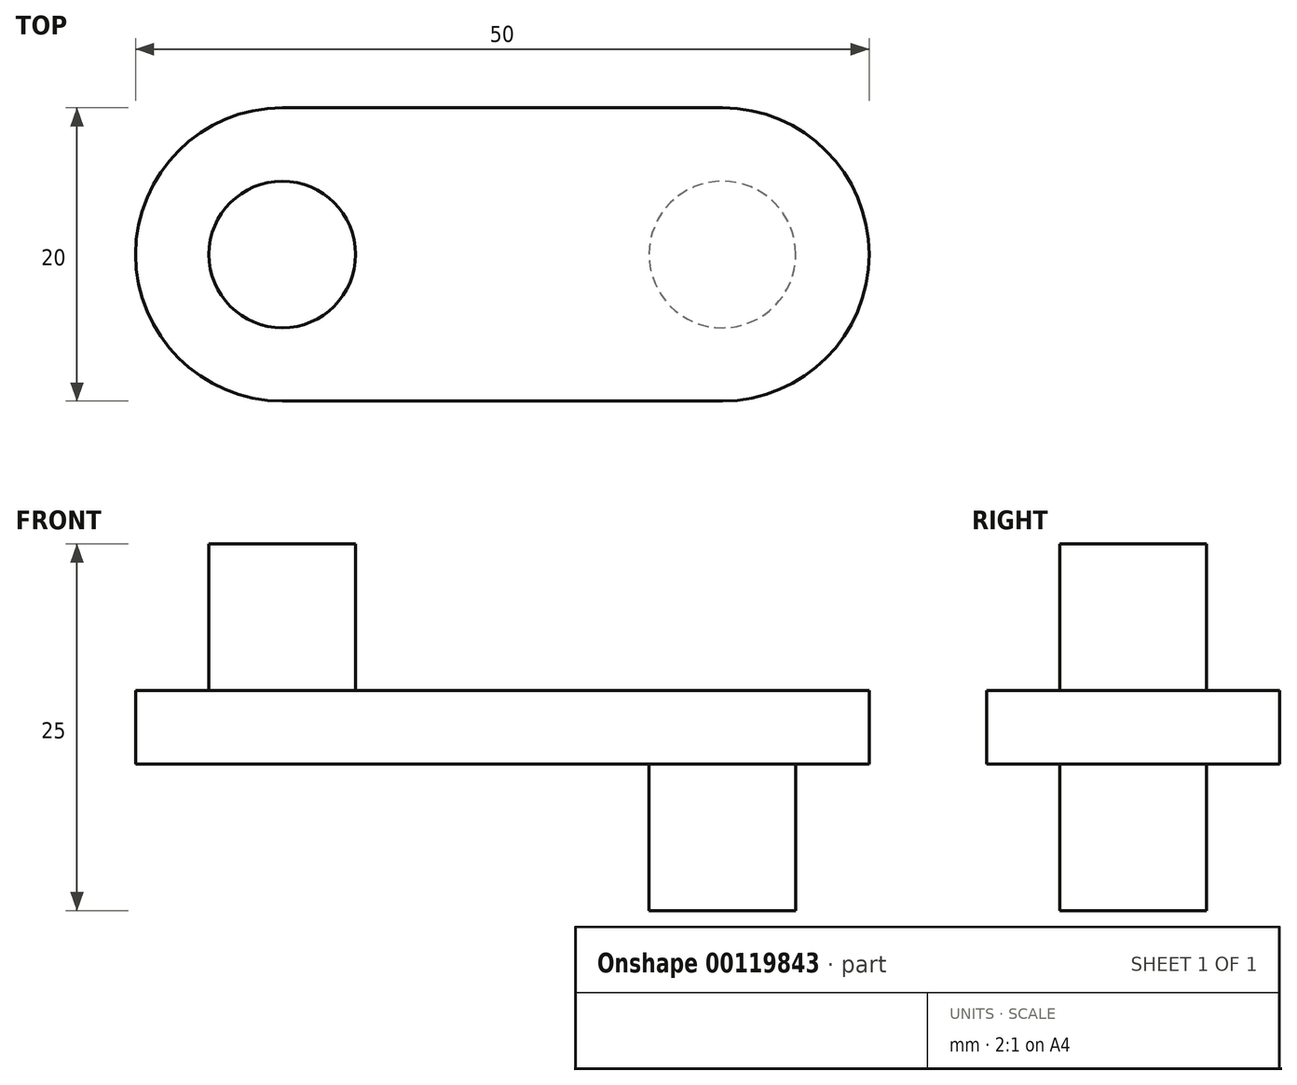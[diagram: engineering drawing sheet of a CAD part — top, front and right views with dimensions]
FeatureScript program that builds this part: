
annotation { "Feature Type Name" : "Feature", "Feature Type Description" : "" }
export const myFeature = defineFeature(function(context is Context, id is Id, definition is map)
    precondition{}
    {
        {
            var Q0;
            Q0=qCreatedBy(makeId("Top.planeOp"),FACE);
            var sketch = newSketch(context, id + "F0", { "sketchPlane" : qUnion([Q0])});
            skLineSegment(sketch, "E0", {"start": v(0, 43) * mm, "end": v(0, -24.5) * mm, "construction": true});
            skLineSegment(sketch, "E1", {"start": v(-26.57, 0) * mm, "end": v(38.25, 0) * mm, "construction": true});
            skLineSegment(sketch, "E2", {"start": v(0, 0) * mm, "end": v(30, 0) * mm});
            skLineSegment(sketch, "E3", {"start": v(0, 20) * mm, "end": v(30, 20) * mm});
            skLineSegment(sketch, "E4", {"start": v(30, 35.47) * mm, "end": v(30, -14.28) * mm, "construction": true});
            skArc(sketch, "E5", {"start": v(0, 20) * mm, "mid": v(-10, 10) * mm, "end": v(0, 0) * mm});
            skArc(sketch, "E6", {"start": v(30, 0) * mm, "mid": v(40, 10) * mm, "end": v(30, 20) * mm});
            skCircle(sketch, "E7", {"center": v(0, 10) * mm, "radius": 5 * mm});
            skCircle(sketch, "E8", {"center": v(30, 10) * mm, "radius": 5 * mm});
            skSolve(sketch);
        }
        {
            var Q0;
            Q0=makeQuery(id+"F0.imprint","IMPRINT",FACE,{"disambiguationData":[TD([[makeQuery(id+"F0.imprint","IMPRINT",EDGE,{"derivedFrom":sQuery(id+"F0.wireOp",EDGE,"E2")}),1.0]])]});
            extrude(context, id + "F1", {"entities" : qUnion([Q0]), "depth" : 5 * mm});
        }
        {
            var Q0;
            Q0=makeQuery(id+"F0.imprint","IMPRINT",FACE,{"disambiguationData":[TD([[makeQuery(id+"F0.imprint","IMPRINT",EDGE,{"derivedFrom":sQuery(id+"F0.wireOp",EDGE,"E7")}),1.0]])]});
            extrude(context, id + "F2", {"entities" : qUnion([Q0]), "operationType" : NewBodyOperationType.ADD, "depth" : 15 * mm});
        }
        {
            var Q0;
            Q0=makeQuery(id+"F0.imprint","IMPRINT",FACE,{"disambiguationData":[TD([[makeQuery(id+"F0.imprint","IMPRINT",EDGE,{"derivedFrom":sQuery(id+"F0.wireOp",EDGE,"E8")}),1.0]])]});
            var Q1;
            Q1=makeQuery(id+"F1.opExtrude","CAP_FACE",FACE,{"disambiguationData":[OSD([sQuery(id+"F0.wireOp",EDGE,"E2"),sQuery(id+"F0.wireOp",EDGE,"E3"),sQuery(id+"F0.wireOp",EDGE,"E5"),sQuery(id+"F0.wireOp",EDGE,"E6"),sQuery(id+"F0.wireOp",EDGE,"E7"),sQuery(id+"F0.wireOp",EDGE,"E8")])],"isStart":false});
            extrude(context, id + "F3", {"entities" : qUnion([Q0]), "operationType" : NewBodyOperationType.ADD, "oppositeDirection" : true, "depth" : 10 * mm, "hasSecondDirection" : true, "secondDirectionBound" : SecondDirectionBoundingType.UP_TO_SURFACE, "secondDirectionOppositeDirection" : false, "secondDirectionBoundEntityFace" : qUnion([Q1]), "secondDirectionDepth" : 25 * mm});
        }
    });
